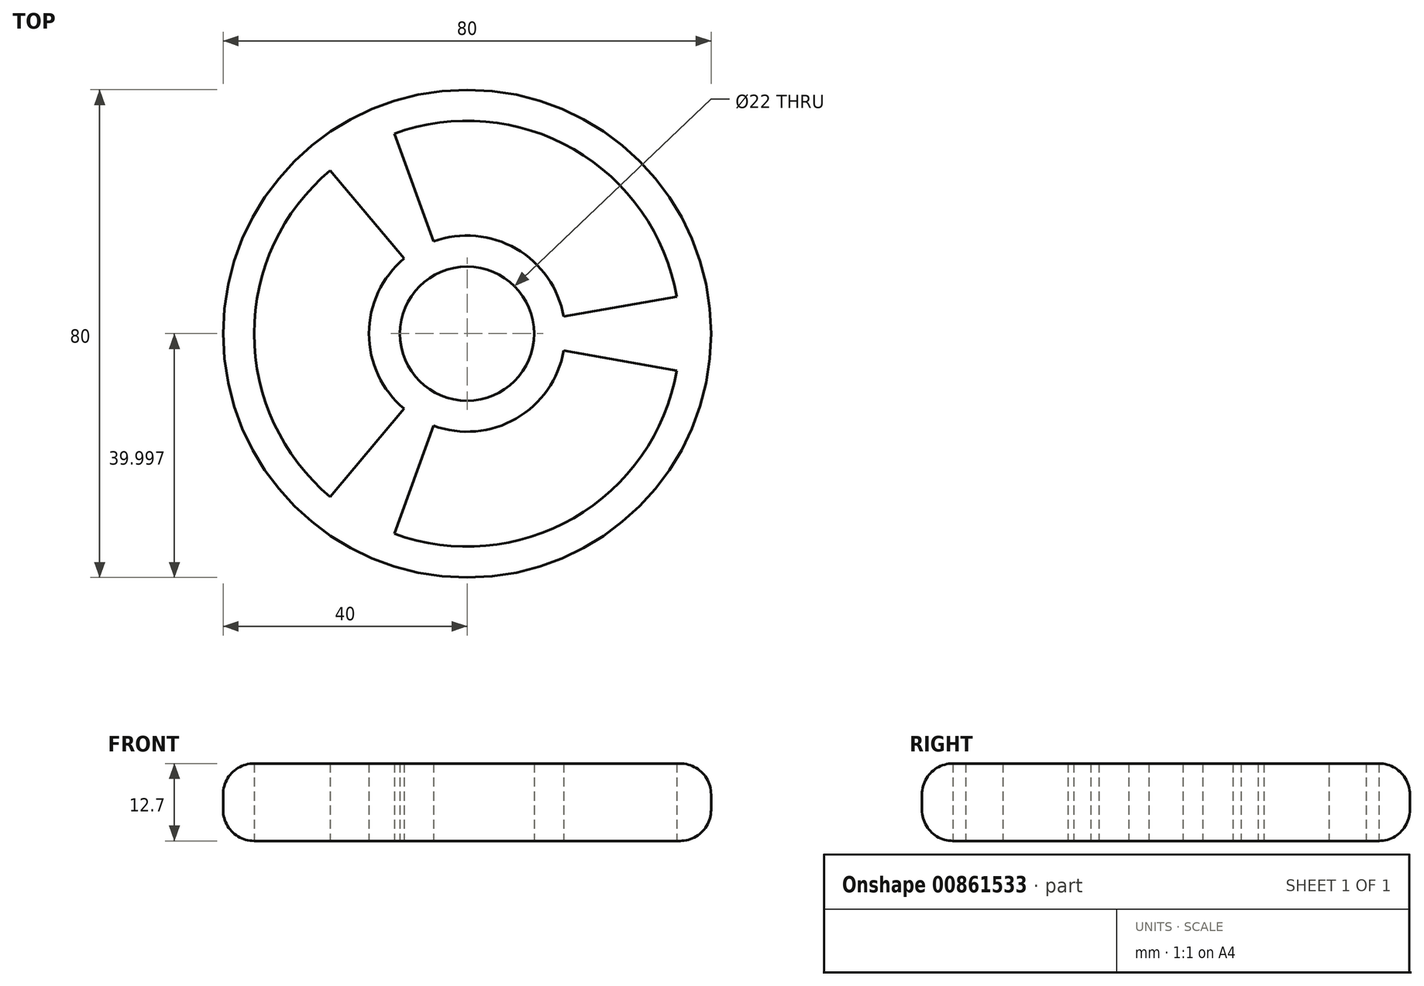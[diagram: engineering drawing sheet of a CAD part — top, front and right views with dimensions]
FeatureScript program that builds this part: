
annotation { "Feature Type Name" : "Feature", "Feature Type Description" : "" }
export const myFeature = defineFeature(function(context is Context, id is Id, definition is map)
    precondition{}
    {
        {
            var Q0;
            Q0=qCreatedBy(makeId("Top.planeOp"),FACE);
            var sketch = newSketch(context, id + "F0", { "sketchPlane" : qUnion([Q0])});
            skCircle(sketch, "E0", {"center": v(-4.68, 26.1) * mm, "radius": 11 * mm});
            skCircle(sketch, "E1", {"center": v(-4.68, 26.1) * mm, "radius": 16.08 * mm});
            skCircle(sketch, "E2", {"center": v(-4.68, 26.1) * mm, "radius": 40 * mm});
            skCircle(sketch, "E3", {"center": v(-4.68, 26.1) * mm, "radius": 34.92 * mm});
            skLineSegment(sketch, "E4", {"start": v(-4.68, 26.1) * mm, "end": v(34.71, 33.05) * mm});
            skLineSegment(sketch, "E5.MirrorCS", {"start": v(-4.68, 26.1) * mm, "end": v(34.71, 19.16) * mm});
            skLineSegment(sketch, "E6.1.0", {"start": v(-4.68, 26.1) * mm, "end": v(-18.36, -11.48) * mm});
            skLineSegment(sketch, "E6.1.1", {"start": v(-4.68, 26.1) * mm, "end": v(-30.4, -4.54) * mm});
            skLineSegment(sketch, "E6.2.0", {"start": v(-4.68, 26.1) * mm, "end": v(-30.4, 56.75) * mm});
            skLineSegment(sketch, "E6.2.1", {"start": v(-4.68, 26.1) * mm, "end": v(-18.36, 63.7) * mm});
            skLineSegment(sketch, "E6.anchor1", {"start": v(-4.68, 26.1) * mm, "end": v(34.71, 19.16) * mm, "construction": true});
            skLineSegment(sketch, "E6.anchor2", {"start": v(-4.68, 26.1) * mm, "end": v(-18.36, 63.7) * mm, "construction": true});
            skSolve(sketch);
        }
        {
            var Q0;
            {var subQ0=sQuery(id+"F0.wireOp",EDGE,"E6.2.0");var subQ1=sQuery(id+"F0.wireOp",EDGE,"E2");var subQ2=makeQuery(id+"F0.imprint","INTERSECT",VERTEX,{"derivedFrom":[subQ1,subQ0]});Q0=makeQuery(id+"F0.imprint","IMPRINT",FACE,{"disambiguationData":[TD([[makeQuery(id+"F0.imprint","IMPRINT",EDGE,{"disambiguationData":[TD([[subQ2,1.0]])],"derivedFrom":subQ1}),1.0]])]});}
            var Q1;
            {var subQ0=sQuery(id+"F0.wireOp",EDGE,"E6.1.1");var subQ1=sQuery(id+"F0.wireOp",EDGE,"E2");var subQ2=makeQuery(id+"F0.imprint","INTERSECT",VERTEX,{"derivedFrom":[subQ1,subQ0]});Q1=makeQuery(id+"F0.imprint","IMPRINT",FACE,{"disambiguationData":[TD([[makeQuery(id+"F0.imprint","IMPRINT",EDGE,{"disambiguationData":[TD([[subQ2,1.0]])],"derivedFrom":subQ1}),1.0]])]});}
            var Q2;
            {var subQ0=sQuery(id+"F0.wireOp",EDGE,"E6.1.0");var subQ1=sQuery(id+"F0.wireOp",EDGE,"E2");var subQ2=makeQuery(id+"F0.imprint","INTERSECT",VERTEX,{"derivedFrom":[subQ1,subQ0]});Q2=makeQuery(id+"F0.imprint","IMPRINT",FACE,{"disambiguationData":[TD([[makeQuery(id+"F0.imprint","IMPRINT",EDGE,{"disambiguationData":[TD([[subQ2,1.0]])],"derivedFrom":subQ1}),1.0]])]});}
            var Q3;
            {var subQ0=sQuery(id+"F0.wireOp",EDGE,"E5.MirrorCS");var subQ1=sQuery(id+"F0.wireOp",EDGE,"E2");var subQ2=makeQuery(id+"F0.imprint","INTERSECT",VERTEX,{"derivedFrom":[subQ1,subQ0]});Q3=makeQuery(id+"F0.imprint","IMPRINT",FACE,{"disambiguationData":[TD([[makeQuery(id+"F0.imprint","IMPRINT",EDGE,{"disambiguationData":[TD([[subQ2,1.0]])],"derivedFrom":subQ1}),1.0]])]});}
            var Q4;
            {var subQ0=sQuery(id+"F0.wireOp",EDGE,"E4");var subQ1=sQuery(id+"F0.wireOp",EDGE,"E2");var subQ2=makeQuery(id+"F0.imprint","INTERSECT",VERTEX,{"derivedFrom":[subQ1,subQ0]});Q4=makeQuery(id+"F0.imprint","IMPRINT",FACE,{"disambiguationData":[TD([[makeQuery(id+"F0.imprint","IMPRINT",EDGE,{"disambiguationData":[TD([[subQ2,1.0]])],"derivedFrom":subQ1}),1.0]])]});}
            var Q5;
            {var subQ0=sQuery(id+"F0.wireOp",EDGE,"E6.2.1");var subQ1=sQuery(id+"F0.wireOp",EDGE,"E1");var subQ2=makeQuery(id+"F0.imprint","INTERSECT",VERTEX,{"derivedFrom":[subQ1,subQ0]});Q5=makeQuery(id+"F0.imprint","IMPRINT",FACE,{"disambiguationData":[TD([[makeQuery(id+"F0.imprint","IMPRINT",EDGE,{"disambiguationData":[TD([[subQ2,-1.0]])],"derivedFrom":subQ1}),-1.0]])]});}
            var Q6;
            {var subQ0=sQuery(id+"F0.wireOp",EDGE,"E6.2.1");var subQ1=sQuery(id+"F0.wireOp",EDGE,"E0");var subQ2=makeQuery(id+"F0.imprint","INTERSECT",VERTEX,{"derivedFrom":[subQ1,subQ0]});Q6=makeQuery(id+"F0.imprint","IMPRINT",FACE,{"disambiguationData":[TD([[makeQuery(id+"F0.imprint","IMPRINT",EDGE,{"disambiguationData":[TD([[subQ2,1.0]])],"derivedFrom":subQ1}),-1.0]])]});}
            var Q7;
            {var subQ0=sQuery(id+"F0.wireOp",EDGE,"E6.2.0");var subQ1=sQuery(id+"F0.wireOp",EDGE,"E0");var subQ2=makeQuery(id+"F0.imprint","INTERSECT",VERTEX,{"derivedFrom":[subQ1,subQ0]});Q7=makeQuery(id+"F0.imprint","IMPRINT",FACE,{"disambiguationData":[TD([[makeQuery(id+"F0.imprint","IMPRINT",EDGE,{"disambiguationData":[TD([[subQ2,-1.0]])],"derivedFrom":subQ1}),-1.0]])]});}
            var Q8;
            {var subQ0=sQuery(id+"F0.wireOp",EDGE,"E6.2.1");var subQ1=sQuery(id+"F0.wireOp",EDGE,"E0");var subQ2=makeQuery(id+"F0.imprint","INTERSECT",VERTEX,{"derivedFrom":[subQ1,subQ0]});Q8=makeQuery(id+"F0.imprint","IMPRINT",FACE,{"disambiguationData":[TD([[makeQuery(id+"F0.imprint","IMPRINT",EDGE,{"disambiguationData":[TD([[subQ2,-1.0]])],"derivedFrom":subQ1}),-1.0]])]});}
            var Q9;
            {var subQ0=sQuery(id+"F0.wireOp",EDGE,"E6.1.0");var subQ1=sQuery(id+"F0.wireOp",EDGE,"E0");var subQ2=makeQuery(id+"F0.imprint","INTERSECT",VERTEX,{"derivedFrom":[subQ1,subQ0]});Q9=makeQuery(id+"F0.imprint","IMPRINT",FACE,{"disambiguationData":[TD([[makeQuery(id+"F0.imprint","IMPRINT",EDGE,{"disambiguationData":[TD([[subQ2,-1.0]])],"derivedFrom":subQ1}),-1.0]])]});}
            var Q10;
            {var subQ0=sQuery(id+"F0.wireOp",EDGE,"E4");var subQ1=sQuery(id+"F0.wireOp",EDGE,"E0");var subQ2=makeQuery(id+"F0.imprint","INTERSECT",VERTEX,{"derivedFrom":[subQ1,subQ0]});Q10=makeQuery(id+"F0.imprint","IMPRINT",FACE,{"disambiguationData":[TD([[makeQuery(id+"F0.imprint","IMPRINT",EDGE,{"disambiguationData":[TD([[subQ2,1.0]])],"derivedFrom":subQ1}),-1.0]])]});}
            var Q11;
            {var subQ0=sQuery(id+"F0.wireOp",EDGE,"E6.1.1");var subQ1=sQuery(id+"F0.wireOp",EDGE,"E0");var subQ2=makeQuery(id+"F0.imprint","INTERSECT",VERTEX,{"derivedFrom":[subQ1,subQ0]});Q11=makeQuery(id+"F0.imprint","IMPRINT",FACE,{"disambiguationData":[TD([[makeQuery(id+"F0.imprint","IMPRINT",EDGE,{"disambiguationData":[TD([[subQ2,-1.0]])],"derivedFrom":subQ1}),-1.0]])]});}
            var Q12;
            {var subQ0=sQuery(id+"F0.wireOp",EDGE,"E4");var subQ1=sQuery(id+"F0.wireOp",EDGE,"E2");var subQ2=makeQuery(id+"F0.imprint","INTERSECT",VERTEX,{"derivedFrom":[subQ1,subQ0]});Q12=makeQuery(id+"F0.imprint","IMPRINT",FACE,{"disambiguationData":[TD([[makeQuery(id+"F0.imprint","IMPRINT",EDGE,{"disambiguationData":[TD([[subQ2,-1.0]])],"derivedFrom":subQ1}),1.0]])]});}
            var Q13;
            {var subQ0=sQuery(id+"F0.wireOp",EDGE,"E4");var subQ1=sQuery(id+"F0.wireOp",EDGE,"E1");var subQ2=makeQuery(id+"F0.imprint","INTERSECT",VERTEX,{"derivedFrom":[subQ1,subQ0]});Q13=makeQuery(id+"F0.imprint","IMPRINT",FACE,{"disambiguationData":[TD([[makeQuery(id+"F0.imprint","IMPRINT",EDGE,{"disambiguationData":[TD([[subQ2,1.0]])],"derivedFrom":subQ1}),-1.0]])]});}
            var Q14;
            {var subQ0=sQuery(id+"F0.wireOp",EDGE,"E6.1.1");var subQ1=sQuery(id+"F0.wireOp",EDGE,"E1");var subQ2=makeQuery(id+"F0.imprint","INTERSECT",VERTEX,{"derivedFrom":[subQ1,subQ0]});Q14=makeQuery(id+"F0.imprint","IMPRINT",FACE,{"disambiguationData":[TD([[makeQuery(id+"F0.imprint","IMPRINT",EDGE,{"disambiguationData":[TD([[subQ2,-1.0]])],"derivedFrom":subQ1}),-1.0]])]});}
            extrude(context, id + "F1", {"entities" : qUnion([Q0, Q1, Q2, Q3, Q4, Q5, Q6, Q7, Q8, Q9, Q10, Q11, Q12, Q13, Q14]), "depth" : 12.7 * mm, "offsetDistance" : 25.4 * mm});
        }
        {
            var Q0;
            Q0=makeQuery(id+"F1.opExtrude","CAP_EDGE",EDGE,{"disambiguationData":[OSD([sQuery(id+"F0.wireOp",EDGE,"E2")])],"isStart":false});
            var Q1;
            Q1=makeQuery(id+"F1.opExtrude","CAP_EDGE",EDGE,{"disambiguationData":[OSD([sQuery(id+"F0.wireOp",EDGE,"E2")])],"isStart":true});
            fillet(context, id + "F2", {"entities" : qUnion([Q0, Q1]), "radius" : 5.08 * mm, "tangentPropagation" : true, "allowEdgeOverflow" : false});
        }
    });
